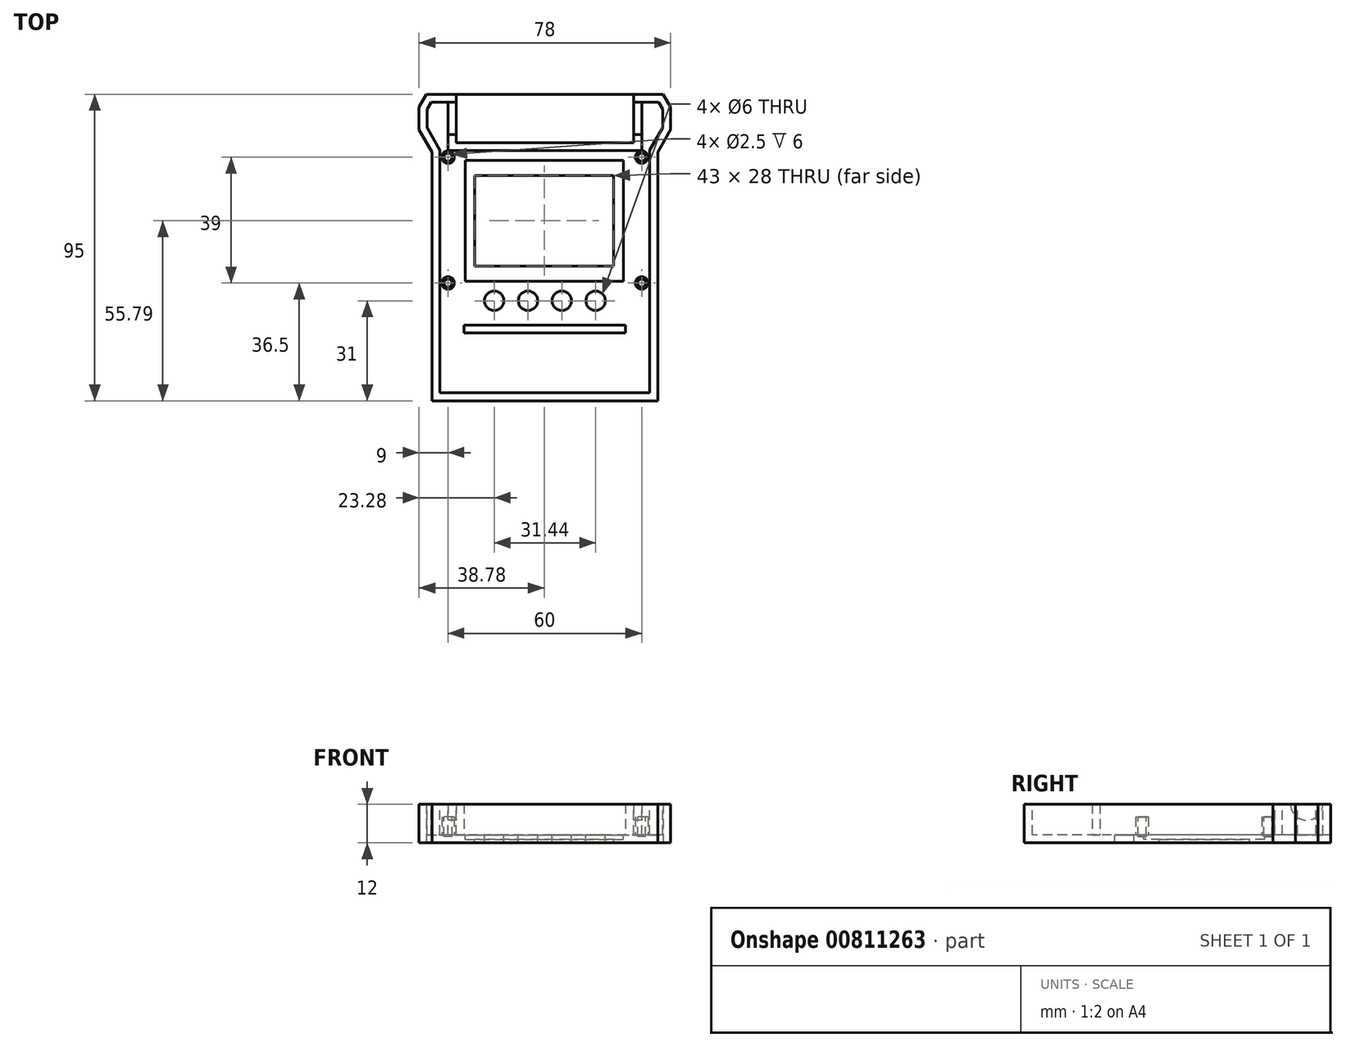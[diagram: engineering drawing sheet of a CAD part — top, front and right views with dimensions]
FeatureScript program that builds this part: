
annotation { "Feature Type Name" : "Feature", "Feature Type Description" : "" }
export const myFeature = defineFeature(function(context is Context, id is Id, definition is map)
    precondition{}
    {
        {
            assignVariable(context, id + "F0", {"name" : "WallThickness", "anyValue" : 2.5});
        }
        {
            var Q0;
            Q0=qCreatedBy(makeId("Top.planeOp"),FACE);
            var sketch = newSketch(context, id + "F1", { "sketchPlane" : qUnion([Q0])});
            skLineSegment(sketch, "E0", {"start": v(-35, -38.5) * mm, "end": v(35, -38.5) * mm});
            skLineSegment(sketch, "E1", {"start": v(35, -38.5) * mm, "end": v(35, 38.5) * mm});
            skLineSegment(sketch, "E2", {"start": v(35, 38.5) * mm, "end": v(39, 45.5) * mm});
            skLineSegment(sketch, "E3", {"start": v(39, 45.5) * mm, "end": v(39, 52.5) * mm});
            skLineSegment(sketch, "E4", {"start": v(-39, 52.5) * mm, "end": v(-39, 45.5) * mm});
            skLineSegment(sketch, "E5", {"start": v(-39, 45.5) * mm, "end": v(-35, 38.5) * mm});
            skLineSegment(sketch, "E6", {"start": v(-35, 38.5) * mm, "end": v(-35, -38.5) * mm});
            skLineSegment(sketch, "E7", {"start": v(-35, 38.5) * mm, "end": v(35, 38.5) * mm, "construction": true});
            skLineSegment(sketch, "E8", {"start": v(-39, 52.5) * mm, "end": v(-36.7, 56.5) * mm});
            skLineSegment(sketch, "E9", {"start": v(-36.7, 56.5) * mm, "end": v(36.7, 56.5) * mm});
            skLineSegment(sketch, "E10", {"start": v(36.7, 56.5) * mm, "end": v(39, 52.5) * mm});
            skSolve(sketch);
        }
        {
            var Q0;
            Q0 = qSketchRegion(id + "F1", true);
            extrude(context, id + "F2", {"entities" : qUnion([Q0]), "depth" : 12 * mm, "offsetDistance" : 25 * mm});
        }
        {
            var Q0;
            Q0=makeQuery(id+"F2.opExtrude","CAP_FACE",FACE,{"disambiguationData":[OSD([sQuery(id+"F1.wireOp",EDGE,"E0"),sQuery(id+"F1.wireOp",EDGE,"E1"),sQuery(id+"F1.wireOp",EDGE,"E2"),sQuery(id+"F1.wireOp",EDGE,"E3"),sQuery(id+"F1.wireOp",EDGE,"E4"),sQuery(id+"F1.wireOp",EDGE,"E5"),sQuery(id+"F1.wireOp",EDGE,"E6"),sQuery(id+"F1.wireOp",EDGE,"E8"),sQuery(id+"F1.wireOp",EDGE,"E9"),sQuery(id+"F1.wireOp",EDGE,"E10")])],"isStart":false});
            var sketch = newSketch(context, id + "F3", { "sketchPlane" : qUnion([Q0])});
            skLineSegment(sketch, "E11.bottom", {"start": v(-27.5, 56.5) * mm, "end": v(27.5, 56.5) * mm});
            skLineSegment(sketch, "E11.top", {"start": v(-27.5, 41.5) * mm, "end": v(27.5, 41.5) * mm});
            skLineSegment(sketch, "E11.left", {"start": v(-27.5, 56.5) * mm, "end": v(-27.5, 41.5) * mm});
            skLineSegment(sketch, "E11.right", {"start": v(27.5, 56.5) * mm, "end": v(27.5, 41.5) * mm});
            skSolve(sketch);
        }
        {
            var Q0;
            Q0 = qSketchRegion(id + "F3", true);
            extrude(context, id + "F4", {"entities" : qUnion([Q0]), "operationType" : NewBodyOperationType.REMOVE, "oppositeDirection" : true, "depth" : 9.5 * mm, "offsetDistance" : 25 * mm});
        }
        {
            var Q0;
            Q0=makeQuery(id+"F2.opExtrude","CAP_FACE",FACE,{"disambiguationData":[OSD([sQuery(id+"F1.wireOp",EDGE,"E0"),sQuery(id+"F1.wireOp",EDGE,"E1"),sQuery(id+"F1.wireOp",EDGE,"E2"),sQuery(id+"F1.wireOp",EDGE,"E3"),sQuery(id+"F1.wireOp",EDGE,"E4"),sQuery(id+"F1.wireOp",EDGE,"E5"),sQuery(id+"F1.wireOp",EDGE,"E6"),sQuery(id+"F1.wireOp",EDGE,"E8"),sQuery(id+"F1.wireOp",EDGE,"E9"),sQuery(id+"F1.wireOp",EDGE,"E10")])],"isStart":false});
            var sketch = newSketch(context, id + "F5", { "sketchPlane" : qUnion([Q0])});
            skLineSegment(sketch, "E12", {"start": v(-32.5, -36) * mm, "end": v(32.5, -36) * mm});
            skLineSegment(sketch, "E13", {"start": v(32.5, -36) * mm, "end": v(32.5, 39.16) * mm});
            skLineSegment(sketch, "E14", {"start": v(32.5, 39.16) * mm, "end": v(36.5, 46.16) * mm});
            skLineSegment(sketch, "E15", {"start": v(36.5, 46.16) * mm, "end": v(36.5, 51.83) * mm});
            skLineSegment(sketch, "E16", {"start": v(36.5, 51.83) * mm, "end": v(35.25, 54) * mm});
            skLineSegment(sketch, "E17", {"start": v(35.25, 54) * mm, "end": v(30, 54) * mm});
            skLineSegment(sketch, "E18", {"start": v(30, 54) * mm, "end": v(30, 39) * mm});
            skLineSegment(sketch, "E19", {"start": v(30, 39) * mm, "end": v(-30, 39) * mm});
            skLineSegment(sketch, "E20", {"start": v(-30, 39) * mm, "end": v(-30, 54) * mm});
            skLineSegment(sketch, "E21", {"start": v(-30, 54) * mm, "end": v(-35.25, 54) * mm});
            skLineSegment(sketch, "E22", {"start": v(-36.5, 46.16) * mm, "end": v(-32.5, 39.16) * mm});
            skLineSegment(sketch, "E23", {"start": v(-32.5, 39.16) * mm, "end": v(-32.5, -36) * mm});
            skLineSegment(sketch, "E24", {"start": v(-32.5, -36) * mm, "end": v(-35, -36) * mm, "construction": true});
            skLineSegment(sketch, "E25", {"start": v(-32.5, -36) * mm, "end": v(-32.5, -38.5) * mm, "construction": true});
            skLineSegment(sketch, "E26", {"start": v(32.5, -36) * mm, "end": v(35, -36) * mm, "construction": true});
            skLineSegment(sketch, "E27", {"start": v(35, 38.5) * mm, "end": v(32.83, 39.74) * mm, "construction": true});
            skLineSegment(sketch, "E28", {"start": v(35.25, 54) * mm, "end": v(37.41, 55.25) * mm, "construction": true});
            skLineSegment(sketch, "E29", {"start": v(30, 54) * mm, "end": v(30, 56.5) * mm, "construction": true});
            skLineSegment(sketch, "E30", {"start": v(30, 54) * mm, "end": v(27.5, 54) * mm, "construction": true});
            skLineSegment(sketch, "E31", {"start": v(27.5, 41.5) * mm, "end": v(27.5, 39) * mm, "construction": true});
            skLineSegment(sketch, "E32", {"start": v(-27.5, 41.5) * mm, "end": v(-30, 41.5) * mm, "construction": true});
            skLineSegment(sketch, "E33", {"start": v(-30, 54) * mm, "end": v(-30, 56.5) * mm, "construction": true});
            skLineSegment(sketch, "E34", {"start": v(-36.5, 46.16) * mm, "end": v(-38.67, 44.92) * mm, "construction": true});
            skLineSegment(sketch, "E35", {"start": v(-35.25, 54) * mm, "end": v(-36.5, 51.83) * mm});
            skLineSegment(sketch, "E36", {"start": v(-36.5, 51.83) * mm, "end": v(-36.5, 46.16) * mm});
            skLineSegment(sketch, "E37", {"start": v(-35.25, 54) * mm, "end": v(-37.41, 55.25) * mm, "construction": true});
            skLineSegment(sketch, "E38", {"start": v(-36.5, 51.83) * mm, "end": v(-39, 51.83) * mm, "construction": true});
            skLineSegment(sketch, "E39", {"start": v(36.5, 46.16) * mm, "end": v(39, 46.16) * mm, "construction": true});
            skSolve(sketch);
        }
        {
            var Q0;
            Q0 = qSketchRegion(id + "F5", true);
            extrude(context, id + "F6", {"entities" : qUnion([Q0]), "operationType" : NewBodyOperationType.REMOVE, "oppositeDirection" : true, "depth" : 9.5 * mm, "offsetDistance" : 25 * mm});
        }
        {
            var Q0;
            Q0=makeQuery(id+"F4.boolean.opBoolean","COPY",FACE,{"derivedFrom":makeQuery(id+"F4.opExtrude","SWEPT_FACE",FACE,{"disambiguationData":[OSD([sQuery(id+"F3.wireOp",EDGE,"E11.left")])]})});
            var sketch = newSketch(context, id + "F7", { "sketchPlane" : qUnion([Q0])});
            skCircle(sketch, "E40", {"center": v(49, 12) * mm, "radius": 5 * mm});
            skSolve(sketch);
        }
        {
            var Q0;
            Q0 = qSketchRegion(id + "F7", true);
            extrude(context, id + "F8", {"entities" : qUnion([Q0]), "operationType" : NewBodyOperationType.REMOVE, "depth" : (55 + getVariable(context, 'WallThickness')) * mm, "offsetDistance" : 25 * mm, "hasSecondDirection" : true, "secondDirectionOppositeDirection" : true, "secondDirectionDepth" : (getVariable(context, 'WallThickness')) * mm});
        }
        {
            var Q0;
            Q0=makeQuery(id+"F6.boolean.opBoolean","COPY",FACE,{"derivedFrom":makeQuery(id+"F6.opExtrude","CAP_FACE",FACE,{"disambiguationData":[OSD([sQuery(id+"F5.wireOp",EDGE,"E12"),sQuery(id+"F5.wireOp",EDGE,"E13"),sQuery(id+"F5.wireOp",EDGE,"E14"),sQuery(id+"F5.wireOp",EDGE,"E15"),sQuery(id+"F5.wireOp",EDGE,"E16"),sQuery(id+"F5.wireOp",EDGE,"E17"),sQuery(id+"F5.wireOp",EDGE,"E18"),sQuery(id+"F5.wireOp",EDGE,"E19"),sQuery(id+"F5.wireOp",EDGE,"E20"),sQuery(id+"F5.wireOp",EDGE,"E21"),sQuery(id+"F5.wireOp",EDGE,"E22"),sQuery(id+"F5.wireOp",EDGE,"E23"),sQuery(id+"F5.wireOp",EDGE,"E35"),sQuery(id+"F5.wireOp",EDGE,"E36")])],"isStart":false})});
            var sketch = newSketch(context, id + "F9", { "sketchPlane" : qUnion([Q0])});
            skLineSegment(sketch, "E41.bottom", {"start": v(-25, -17.5) * mm, "end": v(25, -17.5) * mm});
            skLineSegment(sketch, "E41.top", {"start": v(-25, -15) * mm, "end": v(25, -15) * mm});
            skLineSegment(sketch, "E41.left", {"start": v(-25, -17.5) * mm, "end": v(-25, -15) * mm});
            skLineSegment(sketch, "E41.right", {"start": v(25, -17.5) * mm, "end": v(25, -15) * mm});
            skSolve(sketch);
        }
        {
            var Q0;
            Q0 = qSketchRegion(id + "F9", true);
            extrude(context, id + "F10", {"entities" : qUnion([Q0]), "operationType" : NewBodyOperationType.ADD, "depth" : 9.5 * mm, "offsetDistance" : 25 * mm});
        }
        {
            var Q0;
            Q0=makeQuery(id+"F6.boolean.opBoolean","COPY",FACE,{"derivedFrom":makeQuery(id+"F6.opExtrude","CAP_FACE",FACE,{"disambiguationData":[OSD([sQuery(id+"F5.wireOp",EDGE,"E12"),sQuery(id+"F5.wireOp",EDGE,"E13"),sQuery(id+"F5.wireOp",EDGE,"E14"),sQuery(id+"F5.wireOp",EDGE,"E15"),sQuery(id+"F5.wireOp",EDGE,"E16"),sQuery(id+"F5.wireOp",EDGE,"E17"),sQuery(id+"F5.wireOp",EDGE,"E18"),sQuery(id+"F5.wireOp",EDGE,"E19"),sQuery(id+"F5.wireOp",EDGE,"E20"),sQuery(id+"F5.wireOp",EDGE,"E21"),sQuery(id+"F5.wireOp",EDGE,"E22"),sQuery(id+"F5.wireOp",EDGE,"E23"),sQuery(id+"F5.wireOp",EDGE,"E35"),sQuery(id+"F5.wireOp",EDGE,"E36")])],"isStart":false})});
            var sketch = newSketch(context, id + "F11", { "sketchPlane" : qUnion([Q0])});
            skLineSegment(sketch, "E42.bottom", {"start": v(-32.5, 39) * mm, "end": v(32.5, 39) * mm, "construction": true});
            skLineSegment(sketch, "E42.top", {"start": v(-32.5, -4.5) * mm, "end": v(32.5, -4.5) * mm, "construction": true});
            skLineSegment(sketch, "E42.left", {"start": v(-32.5, 39) * mm, "end": v(-32.5, -4.5) * mm, "construction": true});
            skLineSegment(sketch, "E42.right", {"start": v(32.5, 39) * mm, "end": v(32.5, -4.5) * mm, "construction": true});
            skLineSegment(sketch, "E43.bottom", {"start": v(-21.72, 31.29) * mm, "end": v(21.28, 31.29) * mm});
            skLineSegment(sketch, "E43.top", {"start": v(-21.72, 3.29) * mm, "end": v(21.28, 3.29) * mm});
            skLineSegment(sketch, "E43.left", {"start": v(-21.72, 31.29) * mm, "end": v(-21.72, 3.29) * mm});
            skLineSegment(sketch, "E43.right", {"start": v(21.28, 31.29) * mm, "end": v(21.28, 3.29) * mm});
            skCircle(sketch, "E44", {"center": v(-15.72, -7.5) * mm, "radius": 3 * mm});
            skCircle(sketch, "E45", {"center": v(-5.24, -7.5) * mm, "radius": 3 * mm});
            skCircle(sketch, "E46", {"center": v(5.24, -7.5) * mm, "radius": 3 * mm});
            skCircle(sketch, "E47", {"center": v(15.72, -7.5) * mm, "radius": 3 * mm});
            skLineSegment(sketch, "E48", {"start": v(-15.72, -7.5) * mm, "end": v(-5.24, -7.5) * mm, "construction": true});
            skLineSegment(sketch, "E49", {"start": v(-5.24, -7.5) * mm, "end": v(5.24, -7.5) * mm, "construction": true});
            skLineSegment(sketch, "E50", {"start": v(5.24, -7.5) * mm, "end": v(15.72, -7.5) * mm, "construction": true});
            skLineSegment(sketch, "E51", {"start": v(-21.72, 3.29) * mm, "end": v(-21.72, -7.5) * mm, "construction": true});
            skLineSegment(sketch, "E52", {"start": v(-15.72, -7.5) * mm, "end": v(-21.72, -7.5) * mm, "construction": true});
            skSolve(sketch);
        }
        {
            var Q0;
            Q0 = qSketchRegion(id + "F11", true);
            extrude(context, id + "F12", {"entities" : qUnion([Q0]), "operationType" : NewBodyOperationType.REMOVE, "endBound" : BoundingType.UP_TO_NEXT, "oppositeDirection" : true, "depth" : 25 * mm, "offsetDistance" : 25 * mm});
        }
        {
            var Q0;
            Q0=makeQuery(id+"F6.boolean.opBoolean","COPY",FACE,{"derivedFrom":makeQuery(id+"F6.opExtrude","CAP_FACE",FACE,{"disambiguationData":[OSD([sQuery(id+"F5.wireOp",EDGE,"E12"),sQuery(id+"F5.wireOp",EDGE,"E13"),sQuery(id+"F5.wireOp",EDGE,"E14"),sQuery(id+"F5.wireOp",EDGE,"E15"),sQuery(id+"F5.wireOp",EDGE,"E16"),sQuery(id+"F5.wireOp",EDGE,"E17"),sQuery(id+"F5.wireOp",EDGE,"E18"),sQuery(id+"F5.wireOp",EDGE,"E19"),sQuery(id+"F5.wireOp",EDGE,"E20"),sQuery(id+"F5.wireOp",EDGE,"E21"),sQuery(id+"F5.wireOp",EDGE,"E22"),sQuery(id+"F5.wireOp",EDGE,"E23"),sQuery(id+"F5.wireOp",EDGE,"E35"),sQuery(id+"F5.wireOp",EDGE,"E36")])],"isStart":false})});
            var sketch = newSketch(context, id + "F13", { "sketchPlane" : qUnion([Q0])});
            skLineSegment(sketch, "E53.bottom", {"start": v(-32.5, 39) * mm, "end": v(32.5, 39) * mm, "construction": true});
            skLineSegment(sketch, "E53.top", {"start": v(-32.5, -4.5) * mm, "end": v(32.5, -4.5) * mm, "construction": true});
            skLineSegment(sketch, "E53.left", {"start": v(-32.5, 39) * mm, "end": v(-32.5, -4.5) * mm, "construction": true});
            skLineSegment(sketch, "E53.right", {"start": v(32.5, 39) * mm, "end": v(32.5, -4.5) * mm, "construction": true});
            skLineSegment(sketch, "E54.bottom", {"start": v(-24.72, 36.04) * mm, "end": v(24.28, 36.04) * mm});
            skLineSegment(sketch, "E54.top", {"start": v(-24.72, -1.46) * mm, "end": v(24.28, -1.46) * mm});
            skLineSegment(sketch, "E54.left", {"start": v(-24.72, 36.04) * mm, "end": v(-24.72, -1.46) * mm});
            skLineSegment(sketch, "E54.right", {"start": v(24.28, 36.04) * mm, "end": v(24.28, -1.46) * mm});
            skLineSegment(sketch, "E55", {"start": v(-24.72, 36.04) * mm, "end": v(-21.72, 31.29) * mm, "construction": true});
            skLineSegment(sketch, "E56", {"start": v(24.28, 36.04) * mm, "end": v(21.28, 31.29) * mm, "construction": true});
            skLineSegment(sketch, "E57", {"start": v(24.28, -1.46) * mm, "end": v(21.28, 3.29) * mm, "construction": true});
            skLineSegment(sketch, "E58", {"start": v(-24.72, -1.46) * mm, "end": v(-21.72, 3.29) * mm, "construction": true});
            skSolve(sketch);
        }
        {
            var Q0;
            Q0 = qSketchRegion(id + "F13", true);
            extrude(context, id + "F14", {"entities" : qUnion([Q0]), "operationType" : NewBodyOperationType.REMOVE, "oppositeDirection" : true, "depth" : 1.5 * mm, "offsetDistance" : 25 * mm});
        }
        {
            var Q0;
            Q0=makeQuery(id+"F6.boolean.opBoolean","COPY",FACE,{"derivedFrom":makeQuery(id+"F6.opExtrude","CAP_FACE",FACE,{"disambiguationData":[OSD([sQuery(id+"F5.wireOp",EDGE,"E12"),sQuery(id+"F5.wireOp",EDGE,"E13"),sQuery(id+"F5.wireOp",EDGE,"E14"),sQuery(id+"F5.wireOp",EDGE,"E15"),sQuery(id+"F5.wireOp",EDGE,"E16"),sQuery(id+"F5.wireOp",EDGE,"E17"),sQuery(id+"F5.wireOp",EDGE,"E18"),sQuery(id+"F5.wireOp",EDGE,"E19"),sQuery(id+"F5.wireOp",EDGE,"E20"),sQuery(id+"F5.wireOp",EDGE,"E21"),sQuery(id+"F5.wireOp",EDGE,"E22"),sQuery(id+"F5.wireOp",EDGE,"E23"),sQuery(id+"F5.wireOp",EDGE,"E35"),sQuery(id+"F5.wireOp",EDGE,"E36")])],"isStart":false})});
            var sketch = newSketch(context, id + "F15", { "sketchPlane" : qUnion([Q0])});
            skLineSegment(sketch, "E59.bottom", {"start": v(-32.5, 39) * mm, "end": v(32.5, 39) * mm, "construction": true});
            skLineSegment(sketch, "E59.top", {"start": v(-32.5, -4.5) * mm, "end": v(32.5, -4.5) * mm, "construction": true});
            skLineSegment(sketch, "E59.left", {"start": v(-32.5, 39) * mm, "end": v(-32.5, -4.5) * mm, "construction": true});
            skLineSegment(sketch, "E59.right", {"start": v(32.5, 39) * mm, "end": v(32.5, -4.5) * mm, "construction": true});
            skCircle(sketch, "E60", {"center": v(-30, 37) * mm, "radius": 1.95 * mm});
            skCircle(sketch, "E61", {"center": v(30, 37) * mm, "radius": 1.95 * mm});
            skCircle(sketch, "E62", {"center": v(-30, -2) * mm, "radius": 1.95 * mm});
            skCircle(sketch, "E63", {"center": v(30, -2) * mm, "radius": 1.95 * mm});
            skLineSegment(sketch, "E64", {"start": v(30, -2) * mm, "end": v(30, 37) * mm, "construction": true});
            skLineSegment(sketch, "E65", {"start": v(30, 37) * mm, "end": v(-30, 37) * mm, "construction": true});
            skLineSegment(sketch, "E66", {"start": v(-30, 37) * mm, "end": v(-30, -2) * mm, "construction": true});
            skLineSegment(sketch, "E67", {"start": v(-30, -2) * mm, "end": v(30, -2) * mm, "construction": true});
            skSolve(sketch);
        }
        {
            var Q0;
            Q0 = qSketchRegion(id + "F15", true);
            extrude(context, id + "F16", {"entities" : qUnion([Q0]), "operationType" : NewBodyOperationType.ADD, "depth" : 5.5 * mm, "offsetDistance" : 25 * mm});
        }
        {
            var Q0;
            Q0=makeQuery(id+"F16.opExtrude","CAP_FACE",FACE,{"disambiguationData":[OSD([sQuery(id+"F15.wireOp",EDGE,"E60")])],"isStart":false});
            var sketch = newSketch(context, id + "F17", { "sketchPlane" : qUnion([Q0])});
            skCircle(sketch, "E68", {"center": v(-30, 37) * mm, "radius": 1.25 * mm});
            skCircle(sketch, "E69", {"center": v(30, 37) * mm, "radius": 1.25 * mm});
            skCircle(sketch, "E70", {"center": v(30, -2) * mm, "radius": 1.25 * mm});
            skCircle(sketch, "E71", {"center": v(-30, -2) * mm, "radius": 1.25 * mm});
            skLineSegment(sketch, "E72", {"start": v(-30, 37) * mm, "end": v(30, 37) * mm, "construction": true});
            skLineSegment(sketch, "E73", {"start": v(-30, 37) * mm, "end": v(-30, -2) * mm, "construction": true});
            skLineSegment(sketch, "E74", {"start": v(-30, -2) * mm, "end": v(30, -2) * mm, "construction": true});
            skLineSegment(sketch, "E75", {"start": v(30, 37) * mm, "end": v(30, -2) * mm, "construction": true});
            skSolve(sketch);
        }
        {
            var Q0;
            Q0 = qSketchRegion(id + "F17", true);
            extrude(context, id + "F18", {"entities" : qUnion([Q0]), "operationType" : NewBodyOperationType.REMOVE, "oppositeDirection" : true, "depth" : 6 * mm, "offsetDistance" : 25 * mm});
        }
    });
